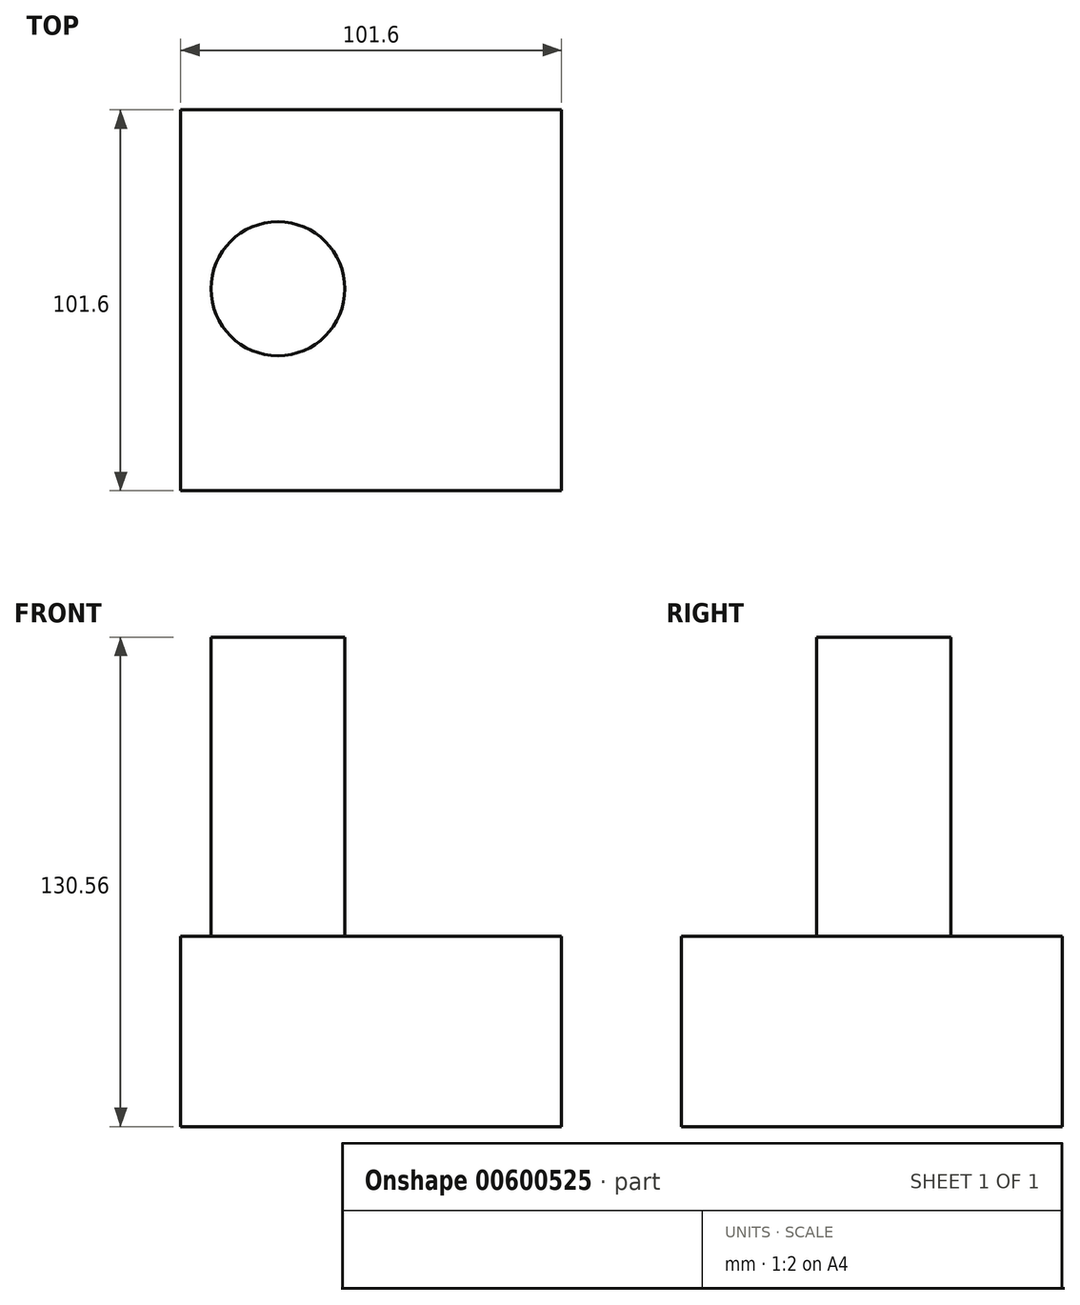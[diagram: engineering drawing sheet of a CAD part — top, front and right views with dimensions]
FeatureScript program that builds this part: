
annotation { "Feature Type Name" : "Feature", "Feature Type Description" : "" }
export const myFeature = defineFeature(function(context is Context, id is Id, definition is map)
    precondition{}
    {
        {
            var Q0;
            Q0=qCreatedBy(makeId("Front.planeOp"),FACE);
            var sketch = newSketch(context, id + "F0", { "sketchPlane" : qUnion([Q0])});
            skLineSegment(sketch, "E0", {"start": v(-50.8, 25.4) * mm, "end": v(-50.8, -25.4) * mm});
            skLineSegment(sketch, "E1", {"start": v(-50.8, -25.4) * mm, "end": v(50.8, -25.4) * mm});
            skLineSegment(sketch, "E2", {"start": v(50.8, -25.4) * mm, "end": v(50.8, 25.4) * mm});
            skLineSegment(sketch, "E3", {"start": v(50.8, 25.4) * mm, "end": v(-50.8, 25.4) * mm});
            skSolve(sketch);
        }
        {
            var Q0;
            Q0=makeQuery(id+"F0.imprint","IMPRINT",FACE,{"disambiguationData":[TD([[makeQuery(id+"F0.imprint","IMPRINT",EDGE,{"derivedFrom":sQuery(id+"F0.wireOp",EDGE,"E0")}),1.0]])]});
            extrude(context, id + "F1", {"entities" : qUnion([Q0]), "depth" : 101.6 * mm, "offsetDistance" : 25.4 * mm});
        }
        {
            var Q0;
            Q0=makeQuery(id+"F1.opExtrude","SWEPT_FACE",FACE,{"disambiguationData":[OSD([sQuery(id+"F0.wireOp",EDGE,"E3")])]});
            var sketch = newSketch(context, id + "F2", { "sketchPlane" : qUnion([Q0])});
            skCircle(sketch, "E4", {"center": v(-24.88, -47.7) * mm, "radius": 17.87 * mm});
            skSolve(sketch);
        }
        {
            var Q0;
            Q0=makeQuery(id+"F2.imprint","IMPRINT",FACE,{"disambiguationData":[TD([[makeQuery(id+"F2.imprint","IMPRINT",EDGE,{"derivedFrom":sQuery(id+"F2.wireOp",EDGE,"E4")}),1.0]])]});
            extrude(context, id + "F3", {"entities" : qUnion([Q0]), "operationType" : NewBodyOperationType.ADD, "depth" : 79.76 * mm, "offsetDistance" : 25.4 * mm});
        }
    });
